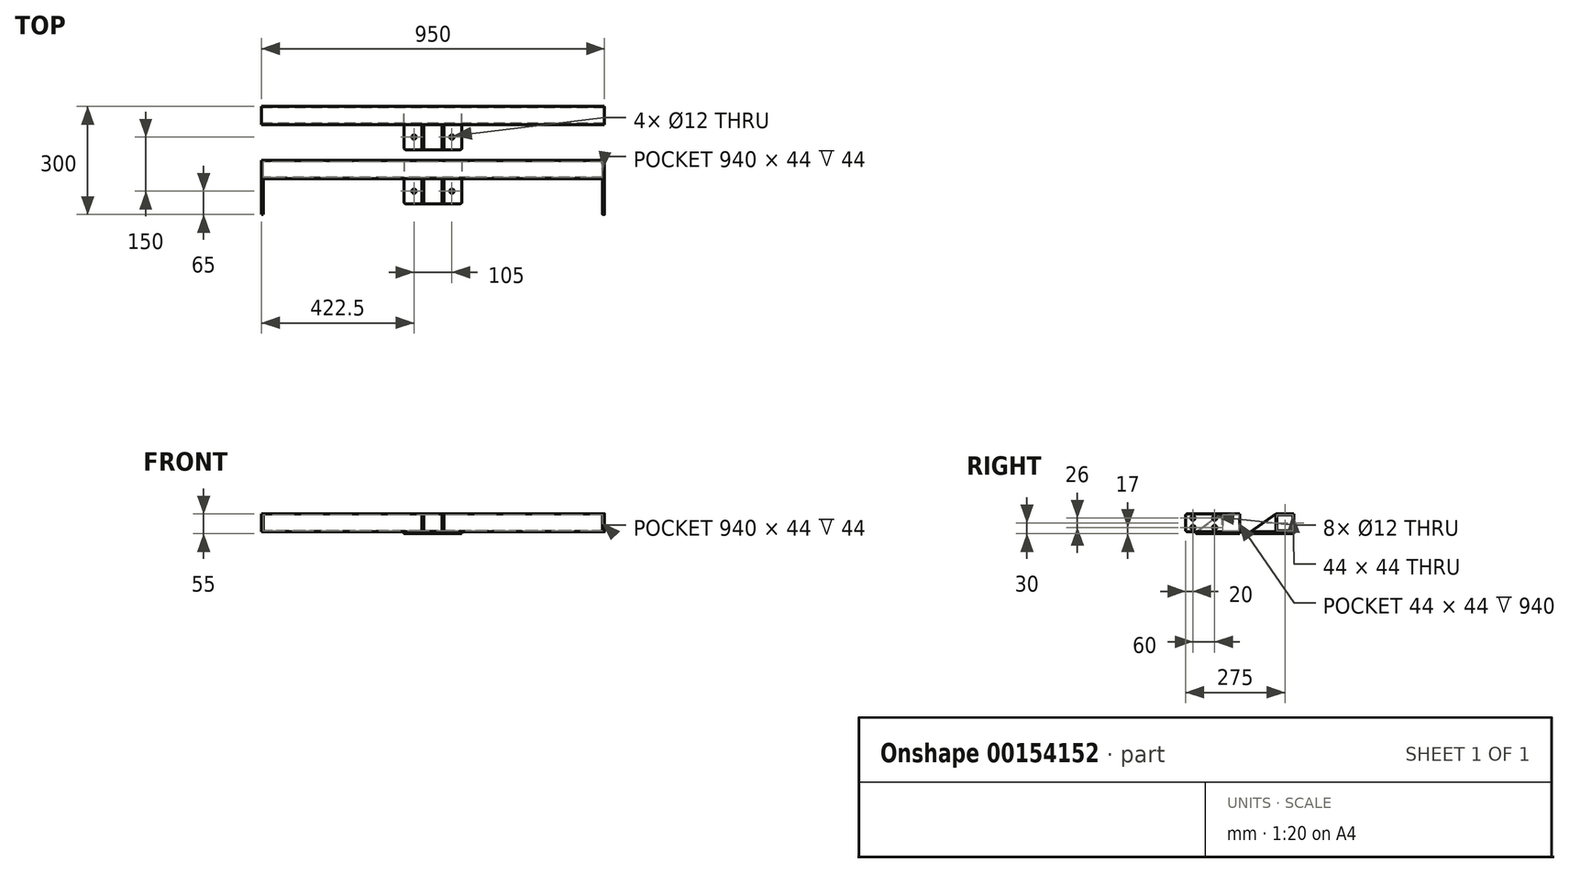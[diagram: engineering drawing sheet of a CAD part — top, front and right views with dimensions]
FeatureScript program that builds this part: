
annotation { "Feature Type Name" : "Feature", "Feature Type Description" : "" }
export const myFeature = defineFeature(function(context is Context, id is Id, definition is map)
    precondition{}
    {
        {
            var Q0;
            Q0=qCreatedBy(makeId("Right.planeOp"),FACE);
            var sketch = newSketch(context, id + "F0", { "sketchPlane" : qUnion([Q0])});
            skLineSegment(sketch, "E0.bottom", {"start": v(-25, 25) * mm, "end": v(25, 25) * mm});
            skLineSegment(sketch, "E0.top", {"start": v(-25, -25) * mm, "end": v(25, -25) * mm});
            skLineSegment(sketch, "E0.left", {"start": v(-25, 25) * mm, "end": v(-25, -25) * mm});
            skLineSegment(sketch, "E0.right", {"start": v(25, 25) * mm, "end": v(25, -25) * mm});
            skPoint(sketch, "E0.middle", {"position": v(0, 0) * mm});
            skLineSegment(sketch, "E1.bottom", {"start": v(-22, 22) * mm, "end": v(22, 22) * mm});
            skLineSegment(sketch, "E1.top", {"start": v(-22, -22) * mm, "end": v(22, -22) * mm});
            skLineSegment(sketch, "E1.left", {"start": v(-22, 22) * mm, "end": v(-22, -22) * mm});
            skLineSegment(sketch, "E1.right", {"start": v(22, 22) * mm, "end": v(22, -22) * mm});
            skSolve(sketch);
        }
        {
            var Q0;
            Q0 = qSketchRegion(id + "F0", true);
            extrude(context, id + "F1", {"entities" : qUnion([Q0]), "depth" : 940 * mm});
        }
        {
            var Q0;
            Q0=makeQuery(id+"F1.opExtrude","CAP_FACE",FACE,{"disambiguationData":[OSD([sQuery(id+"F0.wireOp",EDGE,"E0.bottom"),sQuery(id+"F0.wireOp",EDGE,"E0.top"),sQuery(id+"F0.wireOp",EDGE,"E0.left"),sQuery(id+"F0.wireOp",EDGE,"E0.right"),sQuery(id+"F0.wireOp",EDGE,"E1.bottom"),sQuery(id+"F0.wireOp",EDGE,"E1.top"),sQuery(id+"F0.wireOp",EDGE,"E1.left"),sQuery(id+"F0.wireOp",EDGE,"E1.right")])],"isStart":true});
            var sketch = newSketch(context, id + "F2", { "sketchPlane" : qUnion([Q0])});
            skLineSegment(sketch, "E2.bottom", {"start": v(-25, 25) * mm, "end": v(125, 25) * mm});
            skLineSegment(sketch, "E2.top", {"start": v(-25, -25) * mm, "end": v(125, -25) * mm});
            skLineSegment(sketch, "E2.left", {"start": v(-25, 25) * mm, "end": v(-25, -25) * mm});
            skLineSegment(sketch, "E2.right", {"start": v(125, 25) * mm, "end": v(125, -25) * mm});
            skPoint(sketch, "E3", {"position": v(105, 13) * mm});
            skPoint(sketch, "E4", {"position": v(105, -13) * mm});
            skPoint(sketch, "E5", {"position": v(45, -13) * mm});
            skPoint(sketch, "E6", {"position": v(45, 13) * mm});
            skCircle(sketch, "E7", {"center": v(45, 13) * mm, "radius": 6 * mm});
            skCircle(sketch, "E8", {"center": v(45, -13) * mm, "radius": 6 * mm});
            skCircle(sketch, "E9", {"center": v(105, -13) * mm, "radius": 6 * mm});
            skCircle(sketch, "E10", {"center": v(105, 13) * mm, "radius": 6 * mm});
            skSolve(sketch);
        }
        {
            var Q0;
            Q0 = qSketchRegion(id + "F2", true);
            extrude(context, id + "F3", {"entities" : qUnion([Q0]), "depth" : 5 * mm});
        }
        {
            var Q0;
            Q0=qCreatedBy(makeId("Right.planeOp"),FACE);
            cPlane(context, id + "F4", {"entities" : qUnion([Q0]), "cplaneType" : CPlaneType.OFFSET, "offset" : 470 * mm, "width" : 150 * mm, "height" : 150 * mm});
        }
        {
            var Q0;
            Q0=makeQuery(id+"F3.opExtrude","SWEPT_BODY",BODY,{"disambiguationData":[OSD([sQuery(id+"F2.wireOp",EDGE,"E2.bottom"),sQuery(id+"F2.wireOp",EDGE,"E2.top"),sQuery(id+"F2.wireOp",EDGE,"E2.left"),sQuery(id+"F2.wireOp",EDGE,"E2.right"),sQuery(id+"F2.wireOp",EDGE,"E7"),sQuery(id+"F2.wireOp",EDGE,"E8"),sQuery(id+"F2.wireOp",EDGE,"E9"),sQuery(id+"F2.wireOp",EDGE,"E10")])]});
            var Q1;
            Q1=qCreatedBy(id+"F4.planeOp",FACE);
            mirror(context, id + "F5", {"operationType" : NewBodyOperationType.ADD, "entities" : qUnion([Q0]), "mirrorPlane" : qUnion([Q1])});
        }
        {
            var Q0;
            Q0=makeQuery(id+"F3.opExtrude","SWEPT_EDGE",EDGE,{"disambiguationData":[OSD([sQuery(id+"F2.wireOp",EDGE,"E2.bottom"),sQuery(id+"F2.wireOp",EDGE,"E2.right")])]});
            var Q1;
            Q1=makeQuery(id+"F3.opExtrude","SWEPT_EDGE",EDGE,{"disambiguationData":[OSD([sQuery(id+"F2.wireOp",EDGE,"E2.top"),sQuery(id+"F2.wireOp",EDGE,"E2.right")])]});
            var Q2;
            Q2=makeQuery(id+"F5.opPattern","COPY",EDGE,{"derivedFrom":makeQuery(id+"F3.opExtrude","SWEPT_EDGE",EDGE,{"disambiguationData":[OSD([sQuery(id+"F2.wireOp",EDGE,"E2.bottom"),sQuery(id+"F2.wireOp",EDGE,"E2.right")])]}),"instanceName":"1"});
            var Q3;
            Q3=makeQuery(id+"F5.opPattern","COPY",EDGE,{"derivedFrom":makeQuery(id+"F3.opExtrude","SWEPT_EDGE",EDGE,{"disambiguationData":[OSD([sQuery(id+"F2.wireOp",EDGE,"E2.top"),sQuery(id+"F2.wireOp",EDGE,"E2.right")])]}),"instanceName":"1"});
            fillet(context, id + "F6", {"entities" : qUnion([Q0, Q1, Q2, Q3]), "radius" : 5 * mm, "tangentPropagation" : true, "allowEdgeOverflow" : false});
        }
        {
            var Q0;
            {var subQ0=makeQuery(id+"F3.opExtrude","SWEPT_FACE",FACE,{"disambiguationData":[OSD([sQuery(id+"F2.wireOp",EDGE,"E2.top")])]});Q0=makeQuery(id+"F5.boolean.opBoolean","MERGE",FACE,{"derivedFrom":[makeQuery(id+"F1.opExtrude","SWEPT_FACE",FACE,{"disambiguationData":[OSD([sQuery(id+"F0.wireOp",EDGE,"E0.top")])]}),subQ0,makeQuery(id+"F5.opPattern","COPY",FACE,{"derivedFrom":subQ0,"instanceName":"1"})]});}
            var sketch = newSketch(context, id + "F7", { "sketchPlane" : qUnion([Q0])});
            skPoint(sketch, "E11", {"position": v(470, 0) * mm});
            skPoint(sketch, "E11.positionSnap0", {"position": v(470, 25) * mm});
            skPoint(sketch, "E12", {"position": v(470, -25) * mm});
            skPoint(sketch, "E13", {"position": v(390, -25) * mm});
            skLineSegment(sketch, "E14.bottom", {"start": v(390, -25) * mm, "end": v(550, -25) * mm});
            skLineSegment(sketch, "E14.top", {"start": v(395, 95) * mm, "end": v(545, 95) * mm});
            skLineSegment(sketch, "E14.left", {"start": v(390, -25) * mm, "end": v(390, 90) * mm});
            skLineSegment(sketch, "E14.right", {"start": v(550, -25) * mm, "end": v(550, 90) * mm});
            skPoint(sketch, "E15", {"position": v(470, 60) * mm});
            skLineSegment(sketch, "E16", {"start": v(470, 60) * mm, "end": v(470, -25) * mm, "construction": true});
            skPoint(sketch, "E17.visualSharp", {"position": v(390, 95) * mm});
            skArc(sketch, "E17.filletArc", {"start": v(395, 95) * mm, "mid": v(391.46, 93.54) * mm, "end": v(390, 90) * mm});
            skPoint(sketch, "E18.visualSharp", {"position": v(550, 95) * mm});
            skArc(sketch, "E18.filletArc", {"start": v(550, 90) * mm, "mid": v(548.54, 93.54) * mm, "end": v(545, 95) * mm});
            skPoint(sketch, "E19", {"position": v(417.5, 60) * mm});
            skCircle(sketch, "E20", {"center": v(417.5, 60) * mm, "radius": 6 * mm});
            skCircle(sketch, "E21.MirrorC", {"center": v(522.5, 60) * mm, "radius": 6 * mm});
            skSolve(sketch);
        }
        {
            var Q0;
            Q0 = qSketchRegion(id + "F7", true);
            extrude(context, id + "F8", {"entities" : qUnion([Q0]), "operationType" : NewBodyOperationType.ADD, "depth" : 5 * mm});
        }
        {
            var Q0;
            Q0=makeQuery(id+"F8.opExtrude","CAP_FACE",FACE,{"disambiguationData":[OSD([sQuery(id+"F7.wireOp",EDGE,"E14.bottom"),sQuery(id+"F7.wireOp",EDGE,"E14.top"),sQuery(id+"F7.wireOp",EDGE,"E14.left"),sQuery(id+"F7.wireOp",EDGE,"E14.right"),sQuery(id+"F7.wireOp",EDGE,"m6wKqi57-DuAt-E1DS-QqLw-ufLaUYtHjlNy.bottom"),sQuery(id+"F7.wireOp",EDGE,"m6wKqi57-DuAt-E1DS-QqLw-ufLaUYtHjlNy.top"),sQuery(id+"F7.wireOp",EDGE,"007a8295-09bb-4473-b2f6-c0ea3058d0a8.filletArc"),sQuery(id+"F7.wireOp",EDGE,"79df6df0-9f85-4f5e-96e9-b639f9d556d0.filletArc"),sQuery(id+"F7.wireOp",EDGE,"0128e15e-0f05-424c-b13d-04522cb52e16.filletArc"),sQuery(id+"F7.wireOp",EDGE,"50a278d8-6145-452d-8fc7-20f9416e691b.filletArc"),sQuery(id+"F7.wireOp",EDGE,"87d156b8-daf5-4712-a91e-8e2b0a7db3640.MirrorCS"),sQuery(id+"F7.wireOp",EDGE,"2912dd08-fbbf-4bd3-963f-b497ba566de60.MirrorCS"),sQuery(id+"F7.wireOp",EDGE,"fefc7c1b-f881-4c2b-8fc5-c5ba19187f8d0.MirrorCS"),sQuery(id+"F7.wireOp",EDGE,"ceda12f3-86ca-49ca-8af7-22b0c4f0f7030.MirrorCS"),sQuery(id+"F7.wireOp",EDGE,"3fa80ee8-ebe8-410f-adce-2a64b986b4470.MirrorCS"),sQuery(id+"F7.wireOp",EDGE,"bf032a8f-1d27-4770-b7b6-eefb03745adb0.MirrorCS"),sQuery(id+"F7.wireOp",EDGE,"E17.filletArc"),sQuery(id+"F7.wireOp",EDGE,"E18.filletArc")])],"isStart":true});
            var sketch = newSketch(context, id + "F9", { "sketchPlane" : qUnion([Q0])});
            skPoint(sketch, "E22", {"position": v(470, -95) * mm});
            skPoint(sketch, "E23", {"position": v(445, -95) * mm});
            skLineSegment(sketch, "E24.bottom", {"start": v(445, -95) * mm, "end": v(440, -95) * mm});
            skLineSegment(sketch, "E24.top", {"start": v(445, -25) * mm, "end": v(440, -25) * mm});
            skLineSegment(sketch, "E24.left", {"start": v(445, -95) * mm, "end": v(445, -25) * mm});
            skLineSegment(sketch, "E24.right", {"start": v(440, -95) * mm, "end": v(440, -25) * mm});
            skPoint(sketch, "E25", {"position": v(495, -95) * mm});
            skLineSegment(sketch, "E26.bottom", {"start": v(495, -95) * mm, "end": v(500, -95) * mm});
            skLineSegment(sketch, "E26.top", {"start": v(495, -25) * mm, "end": v(500, -25) * mm});
            skLineSegment(sketch, "E26.left", {"start": v(495, -95) * mm, "end": v(495, -25) * mm});
            skLineSegment(sketch, "E26.right", {"start": v(500, -95) * mm, "end": v(500, -25) * mm});
            skSolve(sketch);
        }
        {
            var Q0;
            Q0 = qSketchRegion(id + "F9", true);
            extrude(context, id + "F10", {"entities" : qUnion([Q0]), "operationType" : NewBodyOperationType.ADD, "depth" : 50 * mm});
        }
        {
            var Q0;
            Q0=makeQuery(id+"F10.opExtrude","SWEPT_FACE",FACE,{"disambiguationData":[OSD([sQuery(id+"F9.wireOp",EDGE,"E24.right")])]});
            var sketch = newSketch(context, id + "F11", { "sketchPlane" : qUnion([Q0])});
            skLineSegment(sketch, "E27.0", {"start": v(95, 25) * mm, "end": v(95, -25) * mm});
            skLineSegment(sketch, "E28.0", {"start": v(95, 25) * mm, "end": v(25, 25) * mm});
            skLineSegment(sketch, "E29", {"start": v(25, 25) * mm, "end": v(95, -25) * mm});
            skSolve(sketch);
        }
        {
            var Q0;
            Q0 = qSketchRegion(id + "F11", true);
            extrude(context, id + "F12", {"entities" : qUnion([Q0]), "operationType" : NewBodyOperationType.REMOVE, "oppositeDirection" : true, "depth" : 110 * mm});
        }
        {
            var Q0;
            Q0=makeQuery(id+"F12.boolean.opBoolean","COPY",EDGE,{"derivedFrom":makeQuery(id+"F12.opExtrude","CAP_EDGE",EDGE,{"disambiguationData":[OSD([sQuery(id+"F11.wireOp",EDGE,"E29")])],"isStart":true})});
            var Q1;
            Q1=makeQuery(id+"F12.boolean.opBoolean","INTERSECT",EDGE,{"derivedFrom":[makeQuery(id+"F10.opExtrude","SWEPT_FACE",FACE,{"disambiguationData":[OSD([sQuery(id+"F9.wireOp",EDGE,"E24.left")])]}),makeQuery(id+"F12.opExtrude","SWEPT_FACE",FACE,{"disambiguationData":[OSD([sQuery(id+"F11.wireOp",EDGE,"E29")])]})]});
            var Q2;
            Q2=makeQuery(id+"F12.boolean.opBoolean","COPY",EDGE,{"derivedFrom":makeQuery(id+"F12.opExtrude","CAP_EDGE",EDGE,{"disambiguationData":[OSD([sQuery(id+"F11.wireOp",EDGE,"E29")])],"isStart":false})});
            var Q3;
            Q3=makeQuery(id+"F12.boolean.opBoolean","INTERSECT",EDGE,{"derivedFrom":[makeQuery(id+"F10.opExtrude","SWEPT_FACE",FACE,{"disambiguationData":[OSD([sQuery(id+"F9.wireOp",EDGE,"E26.left")])]}),makeQuery(id+"F12.opExtrude","SWEPT_FACE",FACE,{"disambiguationData":[OSD([sQuery(id+"F11.wireOp",EDGE,"E29")])]})]});
            chamfer(context, id + "F13", {"entities" : qUnion([Q0, Q1, Q2, Q3]), "width" : 1 * mm, "tangentPropagation" : true});
        }
        {
            var Q0;
            Q0=qCreatedBy(makeId("Right.planeOp"),FACE);
            cPlane(context, id + "F14", {"entities" : qUnion([Q0]), "cplaneType" : CPlaneType.OFFSET, "offset" : 5 * mm, "oppositeDirection" : true, "width" : 150 * mm, "height" : 150 * mm});
        }
        {
            var Q0;
            Q0=qCreatedBy(id+"F14.planeOp",FACE);
            var sketch = newSketch(context, id + "F15", { "sketchPlane" : qUnion([Q0])});
            skPoint(sketch, "E30", {"position": v(150, 0) * mm});
            skLineSegment(sketch, "E31.bottom", {"start": v(125, 25) * mm, "end": v(175, 25) * mm});
            skLineSegment(sketch, "E31.top", {"start": v(125, -25) * mm, "end": v(175, -25) * mm});
            skLineSegment(sketch, "E31.left", {"start": v(125, 25) * mm, "end": v(125, -25) * mm});
            skLineSegment(sketch, "E31.right", {"start": v(175, 25) * mm, "end": v(175, -25) * mm});
            skLineSegment(sketch, "E32.bottom", {"start": v(128, 22) * mm, "end": v(172, 22) * mm});
            skLineSegment(sketch, "E32.top", {"start": v(128, -22) * mm, "end": v(172, -22) * mm});
            skLineSegment(sketch, "E32.left", {"start": v(128, 22) * mm, "end": v(128, -22) * mm});
            skLineSegment(sketch, "E32.right", {"start": v(172, 22) * mm, "end": v(172, -22) * mm});
            skSolve(sketch);
        }
        {
            var Q0;
            Q0 = qSketchRegion(id + "F15", true);
            extrude(context, id + "F16", {"entities" : qUnion([Q0]), "depth" : 950 * mm, "offsetDistance" : 25 * mm});
        }
        {
            var Q0;
            Q0=makeQuery(id+"F16.opExtrude","SWEPT_FACE",FACE,{"disambiguationData":[OSD([sQuery(id+"F15.wireOp",EDGE,"E31.right")])]});
            var sketch = newSketch(context, id + "F17", { "sketchPlane" : qUnion([Q0])});
            skLineSegment(sketch, "E33.0", {"start": v(-390, -30) * mm, "end": v(-390, -25) * mm});
            skLineSegment(sketch, "E34.0", {"start": v(-550, -30) * mm, "end": v(-550, -25) * mm});
            skLineSegment(sketch, "E35.0", {"start": v(-550, -30) * mm, "end": v(-390, -30) * mm});
            skLineSegment(sketch, "E36", {"start": v(-550, -25) * mm, "end": v(-390, -25) * mm});
            skSolve(sketch);
        }
        {
            var Q0;
            Q0 = qSketchRegion(id + "F17", true);
            extrude(context, id + "F18", {"entities" : qUnion([Q0]), "operationType" : NewBodyOperationType.ADD, "oppositeDirection" : true, "depth" : 120 * mm, "offsetDistance" : 25 * mm});
        }
        {
            var Q0;
            Q0=makeQuery(id+"F18.opExtrude","SWEPT_FACE",FACE,{"disambiguationData":[OSD([sQuery(id+"F17.wireOp",EDGE,"E36")])]});
            var sketch = newSketch(context, id + "F19", { "sketchPlane" : qUnion([Q0])});
            skLineSegment(sketch, "E37", {"start": v(470, 125) * mm, "end": v(470, 55) * mm});
            skPoint(sketch, "E38", {"position": v(470, 90) * mm});
            skPoint(sketch, "E39", {"position": v(417.5, 90) * mm});
            skCircle(sketch, "E40", {"center": v(417.5, 90) * mm, "radius": 6 * mm});
            skCircle(sketch, "E41.MirrorC", {"center": v(522.5, 90) * mm, "radius": 6 * mm});
            skSolve(sketch);
        }
        {
            var Q0;
            Q0 = qSketchRegion(id + "F19", true);
            extrude(context, id + "F20", {"entities" : qUnion([Q0]), "operationType" : NewBodyOperationType.REMOVE, "oppositeDirection" : true, "depth" : 25 * mm, "offsetDistance" : 25 * mm});
        }
        {
            var Q0;
            Q0=makeQuery(id+"F16.opExtrude","SWEPT_FACE",FACE,{"disambiguationData":[OSD([sQuery(id+"F15.wireOp",EDGE,"E31.left")])]});
            var sketch = newSketch(context, id + "F21", { "sketchPlane" : qUnion([Q0])});
            skLineSegment(sketch, "E42.0", {"start": v(440, -25) * mm, "end": v(390, -25) * mm});
            skLineSegment(sketch, "E43.0", {"start": v(495, -25) * mm, "end": v(445, -25) * mm});
            skLineSegment(sketch, "E44.0", {"start": v(550, -25) * mm, "end": v(500, -25) * mm});
            skLineSegment(sketch, "E45", {"start": v(440, -25) * mm, "end": v(440, 25) * mm});
            skLineSegment(sketch, "E46", {"start": v(440, 25) * mm, "end": v(445, 25) * mm});
            skLineSegment(sketch, "E47", {"start": v(445, 25) * mm, "end": v(445, -25) * mm});
            skLineSegment(sketch, "E48", {"start": v(445, -25) * mm, "end": v(440, -25) * mm});
            skLineSegment(sketch, "E49", {"start": v(495, -25) * mm, "end": v(495, 25) * mm});
            skLineSegment(sketch, "E50", {"start": v(495, 25) * mm, "end": v(500, 25) * mm});
            skLineSegment(sketch, "E51", {"start": v(500, 25) * mm, "end": v(500, -25) * mm});
            skLineSegment(sketch, "E52", {"start": v(500, -25) * mm, "end": v(495, -25) * mm});
            skSolve(sketch);
        }
        {
            var Q0;
            Q0 = qSketchRegion(id + "F21", true);
            extrude(context, id + "F22", {"entities" : qUnion([Q0]), "operationType" : NewBodyOperationType.ADD, "depth" : 70 * mm, "offsetDistance" : 25 * mm});
        }
        {
            var Q0;
            Q0=makeQuery(id+"F22.opExtrude","SWEPT_FACE",FACE,{"disambiguationData":[OSD([sQuery(id+"F21.wireOp",EDGE,"E45")])]});
            var sketch = newSketch(context, id + "F23", { "sketchPlane" : qUnion([Q0])});
            skLineSegment(sketch, "E53.0", {"start": v(-55, 25) * mm, "end": v(-125, 25) * mm});
            skLineSegment(sketch, "E54.0", {"start": v(-55, -25) * mm, "end": v(-55, 25) * mm});
            skLineSegment(sketch, "E55", {"start": v(-125, 25) * mm, "end": v(-55, -25) * mm});
            skSolve(sketch);
        }
        {
            var Q0;
            Q0 = qSketchRegion(id + "F23", true);
            extrude(context, id + "F24", {"entities" : qUnion([Q0]), "operationType" : NewBodyOperationType.REMOVE, "oppositeDirection" : true, "depth" : 60 * mm, "offsetDistance" : 25 * mm});
        }
        {
            var Q0;
            Q0=makeQuery(id+"F18.opExtrude","CAP_EDGE",EDGE,{"disambiguationData":[OSD([sQuery(id+"F17.wireOp",EDGE,"E33.0")])],"isStart":false});
            var Q1;
            Q1=makeQuery(id+"F18.opExtrude","CAP_EDGE",EDGE,{"disambiguationData":[OSD([sQuery(id+"F17.wireOp",EDGE,"E34.0")])],"isStart":false});
            fillet(context, id + "F25", {"entities" : qUnion([Q0, Q1]), "radius" : 5 * mm, "tangentPropagation" : true, "allowEdgeOverflow" : false});
        }
        {
            var Q0;
            Q0=makeQuery(id+"F24.boolean.opBoolean","INTERSECT",EDGE,{"derivedFrom":[makeQuery(id+"F22.opExtrude","SWEPT_FACE",FACE,{"disambiguationData":[OSD([sQuery(id+"F21.wireOp",EDGE,"E47")])]}),makeQuery(id+"F24.opExtrude","SWEPT_FACE",FACE,{"disambiguationData":[OSD([sQuery(id+"F23.wireOp",EDGE,"E55")])]})]});
            var Q1;
            Q1=makeQuery(id+"F24.boolean.opBoolean","COPY",EDGE,{"derivedFrom":makeQuery(id+"F24.opExtrude","CAP_EDGE",EDGE,{"disambiguationData":[OSD([sQuery(id+"F23.wireOp",EDGE,"E55")])],"isStart":true})});
            var Q2;
            Q2=makeQuery(id+"F24.boolean.opBoolean","COPY",EDGE,{"derivedFrom":makeQuery(id+"F24.opExtrude","CAP_EDGE",EDGE,{"disambiguationData":[OSD([sQuery(id+"F23.wireOp",EDGE,"E55")])],"isStart":false})});
            var Q3;
            Q3=makeQuery(id+"F24.boolean.opBoolean","INTERSECT",EDGE,{"derivedFrom":[makeQuery(id+"F22.opExtrude","SWEPT_FACE",FACE,{"disambiguationData":[OSD([sQuery(id+"F21.wireOp",EDGE,"E49")])]}),makeQuery(id+"F24.opExtrude","SWEPT_FACE",FACE,{"disambiguationData":[OSD([sQuery(id+"F23.wireOp",EDGE,"E55")])]})]});
            chamfer(context, id + "F26", {"entities" : qUnion([Q0, Q1, Q2, Q3]), "width" : 1 * mm, "tangentPropagation" : true});
        }
    });
